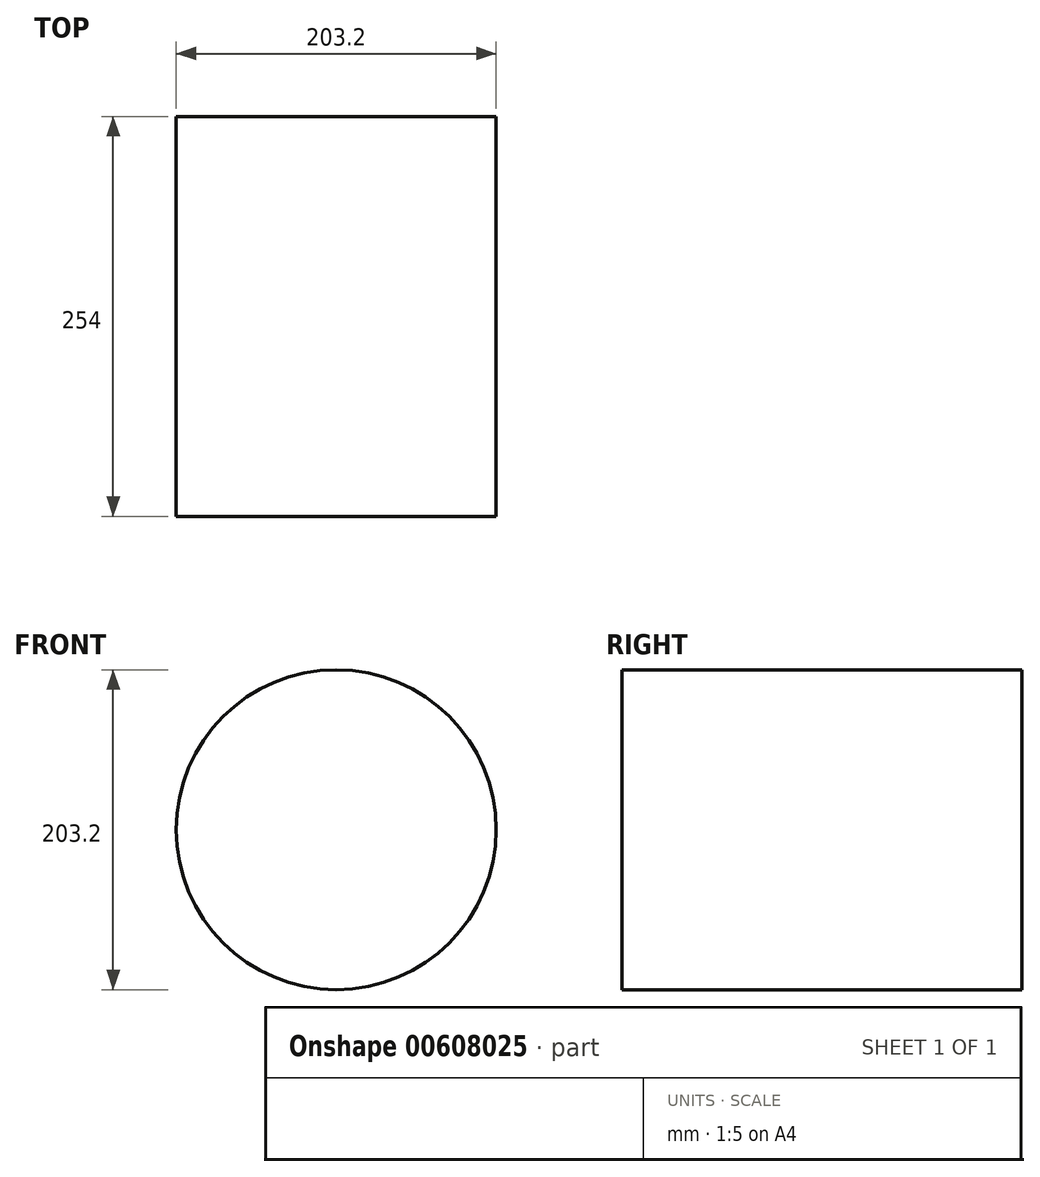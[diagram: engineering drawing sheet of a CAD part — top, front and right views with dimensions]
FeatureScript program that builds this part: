
annotation { "Feature Type Name" : "Feature", "Feature Type Description" : "" }
export const myFeature = defineFeature(function(context is Context, id is Id, definition is map)
    precondition{}
    {
        {
            var Q0;
            Q0=qCreatedBy(makeId("Front.planeOp"),FACE);
            var sketch = newSketch(context, id + "F0", { "sketchPlane" : qUnion([Q0])});
            skCircle(sketch, "E0", {"center": v(-15.2, 0) * mm, "radius": 101.6 * mm});
            skSolve(sketch);
        }
        {
            var Q0;
            Q0 = qSketchRegion(id + "F0", true);
            extrude(context, id + "F1", {"entities" : qUnion([Q0]), "endBound" : BoundingType.SYMMETRIC, "depth" : 254 * mm, "offsetDistance" : 25.4 * mm});
        }
    });
